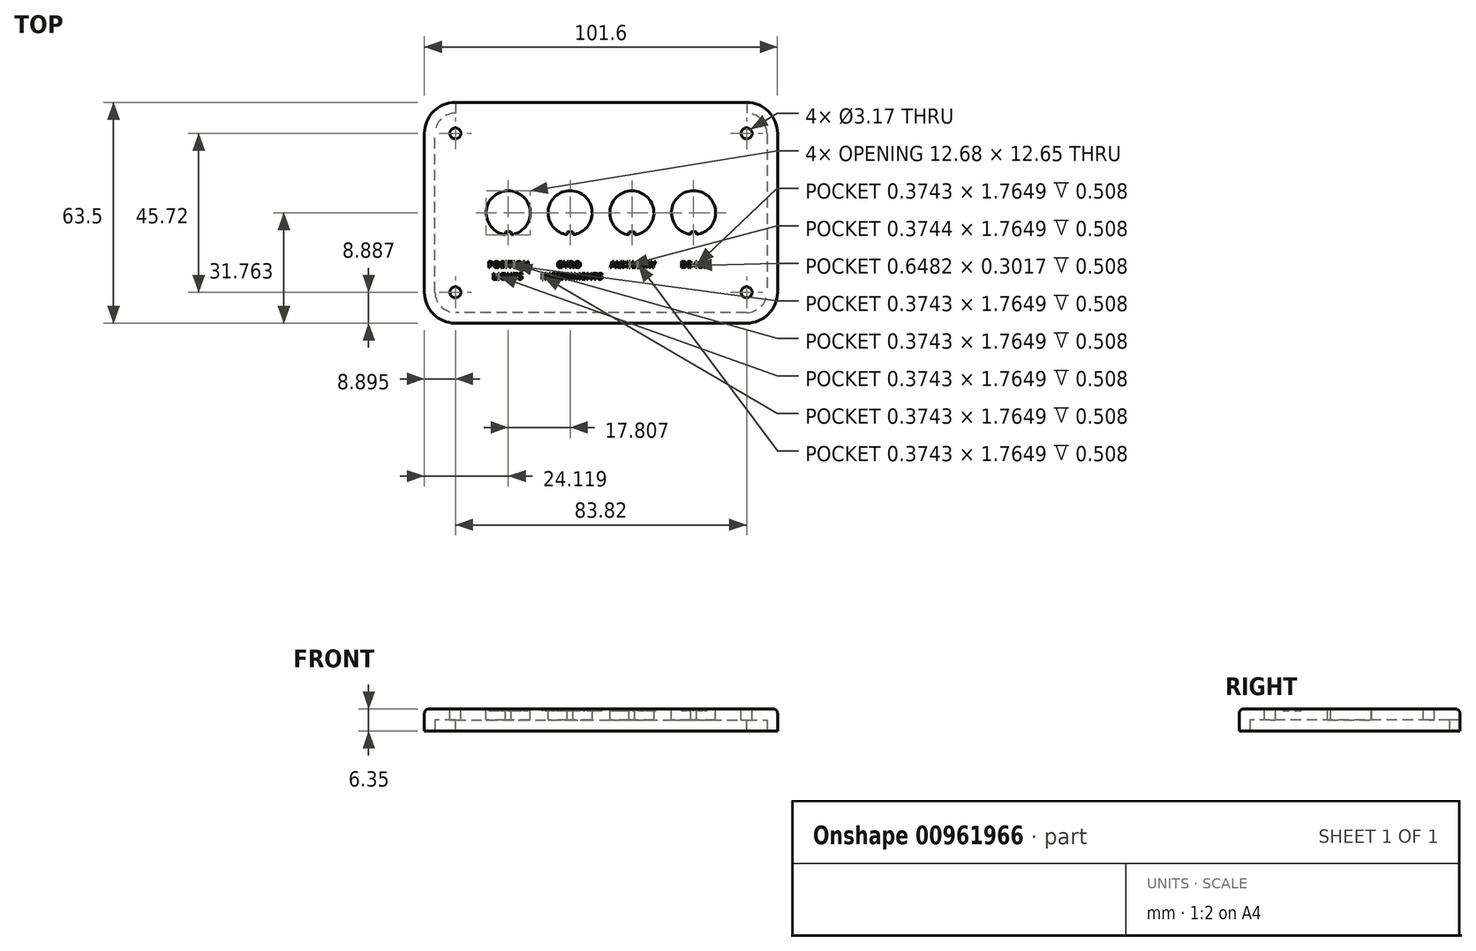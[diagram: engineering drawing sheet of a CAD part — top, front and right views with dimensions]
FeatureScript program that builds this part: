
annotation { "Feature Type Name" : "Feature", "Feature Type Description" : "" }
export const myFeature = defineFeature(function(context is Context, id is Id, definition is map)
    precondition{}
    {
        {
            var Q0;
            Q0=qCreatedBy(makeId("Top.planeOp"),FACE);
            var sketch = newSketch(context, id + "F0", { "sketchPlane" : qUnion([Q0])});
            skPoint(sketch, "E0.middle", {"position": v(-0.12, 0.03) * mm});
            skPoint(sketch, "E1.visualSharp", {"position": v(-44.57, 25.43) * mm});
            skArc(sketch, "E1.filletArc", {"start": v(-42.03, 25.43) * mm, "mid": v(-43.82, 24.68) * mm, "end": v(-44.57, 22.89) * mm});
            skPoint(sketch, "E2.visualSharp", {"position": v(44.33, 25.43) * mm});
            skArc(sketch, "E2.filletArc", {"start": v(44.33, 22.89) * mm, "mid": v(43.6, 24.68) * mm, "end": v(41.8, 25.43) * mm});
            skPoint(sketch, "E3.visualSharp", {"position": v(44.33, -25.37) * mm});
            skArc(sketch, "E3.filletArc", {"start": v(41.8, -25.37) * mm, "mid": v(43.6, -24.63) * mm, "end": v(44.33, -22.83) * mm});
            skPoint(sketch, "E4.visualSharp", {"position": v(-44.57, -25.37) * mm});
            skArc(sketch, "E4.filletArc", {"start": v(-44.57, -22.83) * mm, "mid": v(-43.82, -24.63) * mm, "end": v(-42.03, -25.37) * mm});
            skCircle(sketch, "E5", {"center": v(-42.03, 22.89) * mm, "radius": 1.59 * mm});
            skCircle(sketch, "E6", {"center": v(-42.03, -22.83) * mm, "radius": 1.59 * mm});
            skCircle(sketch, "E7", {"center": v(41.8, -22.83) * mm, "radius": 1.59 * mm});
            skCircle(sketch, "E8", {"center": v(41.8, 22.89) * mm, "radius": 1.59 * mm});
            skArc(sketch, "E9.0", {"start": v(-47.74, -22.83) * mm, "mid": v(-46.07, -26.87) * mm, "end": v(-42.03, -28.55) * mm});
            skLineSegment(sketch, "E9.1", {"start": v(-42.03, -28.55) * mm, "end": v(41.8, -28.55) * mm});
            skLineSegment(sketch, "E9.2", {"start": v(-47.74, -22.83) * mm, "end": v(-47.74, 22.89) * mm});
            skArc(sketch, "E9.3", {"start": v(41.8, -28.55) * mm, "mid": v(45.84, -26.87) * mm, "end": v(47.5, -22.83) * mm});
            skArc(sketch, "E9.4", {"start": v(-42.03, 28.6) * mm, "mid": v(-46.07, 26.93) * mm, "end": v(-47.74, 22.89) * mm});
            skLineSegment(sketch, "E9.5", {"start": v(-42.03, 28.6) * mm, "end": v(41.8, 28.6) * mm});
            skArc(sketch, "E9.6", {"start": v(47.5, 22.89) * mm, "mid": v(45.84, 26.93) * mm, "end": v(41.8, 28.6) * mm});
            skLineSegment(sketch, "E9.7", {"start": v(47.5, -22.83) * mm, "end": v(47.5, 22.89) * mm});
            skArc(sketch, "E10.0", {"start": v(-50.92, -22.83) * mm, "mid": v(-48.31, -29.12) * mm, "end": v(-42.03, -31.72) * mm});
            skLineSegment(sketch, "E10.1", {"start": v(-42.03, -31.72) * mm, "end": v(41.8, -31.72) * mm});
            skLineSegment(sketch, "E10.2", {"start": v(-50.92, -22.83) * mm, "end": v(-50.92, 22.89) * mm});
            skArc(sketch, "E10.3", {"start": v(41.8, -31.72) * mm, "mid": v(48.08, -29.12) * mm, "end": v(50.68, -22.83) * mm});
            skArc(sketch, "E10.4", {"start": v(-42.03, 31.78) * mm, "mid": v(-48.31, 29.17) * mm, "end": v(-50.92, 22.89) * mm});
            skLineSegment(sketch, "E10.5", {"start": v(-42.03, 31.78) * mm, "end": v(41.8, 31.78) * mm});
            skArc(sketch, "E10.6", {"start": v(50.68, 22.89) * mm, "mid": v(48.08, 29.17) * mm, "end": v(41.8, 31.78) * mm});
            skLineSegment(sketch, "E10.7", {"start": v(50.68, -22.83) * mm, "end": v(50.68, 22.89) * mm});
            skPoint(sketch, "E11", {"position": v(-26.79, 0) * mm});
            skPoint(sketch, "E12", {"position": v(-9, 0) * mm});
            skPoint(sketch, "E13", {"position": v(8.77, 0) * mm});
            skPoint(sketch, "E14", {"position": v(26.55, 0) * mm});
            skLineSegment(sketch, "E15.top", {"start": v(27.33, -5.38) * mm, "end": v(25.74, -5.38) * mm});
            skLineSegment(sketch, "E16", {"start": v(25.74, -6.25) * mm, "end": v(25.74, -5.38) * mm});
            skLineSegment(sketch, "E17", {"start": v(27.33, -6.25) * mm, "end": v(27.33, -5.38) * mm});
            skArc(sketch, "E18", {"start": v(27.33, -6.25) * mm, "mid": v(26.54, 6.4) * mm, "end": v(25.74, -6.25) * mm});
            skLineSegment(sketch, "E19.top", {"start": v(9.58, -5.43) * mm, "end": v(7.99, -5.43) * mm});
            skLineSegment(sketch, "E20", {"start": v(7.99, -6.3) * mm, "end": v(7.99, -5.43) * mm});
            skLineSegment(sketch, "E21", {"start": v(9.58, -6.3) * mm, "end": v(9.58, -5.43) * mm});
            skArc(sketch, "E22", {"start": v(9.58, -6.3) * mm, "mid": v(8.78, 6.35) * mm, "end": v(7.99, -6.3) * mm});
            skLineSegment(sketch, "E23.top", {"start": v(-8.2, -5.4) * mm, "end": v(-9.79, -5.4) * mm});
            skLineSegment(sketch, "E24", {"start": v(-9.79, -6.26) * mm, "end": v(-9.79, -5.4) * mm});
            skLineSegment(sketch, "E25", {"start": v(-8.2, -6.26) * mm, "end": v(-8.2, -5.4) * mm});
            skArc(sketch, "E26", {"start": v(-8.2, -6.26) * mm, "mid": v(-9, 6.4) * mm, "end": v(-9.79, -6.26) * mm});
            skLineSegment(sketch, "E27.top", {"start": v(-26, -5.42) * mm, "end": v(-27.6, -5.42) * mm});
            skLineSegment(sketch, "E28", {"start": v(-27.6, -6.28) * mm, "end": v(-27.6, -5.42) * mm});
            skLineSegment(sketch, "E29", {"start": v(-26, -6.28) * mm, "end": v(-26, -5.42) * mm});
            skArc(sketch, "E30", {"start": v(-26, -6.28) * mm, "mid": v(-26.8, 6.37) * mm, "end": v(-27.6, -6.28) * mm});
            skText(sketch, "E31", { "text": "POSITION\n  LIGHTS", "fontName": "OpenSans-Bold.ttf"});
            skText(sketch, "E32", { "text": "       GYRO\nINSTRUMENTS", "fontName": "OpenSans-Bold.ttf"});
            skText(sketch, "E33", { "text": "DE-ICE", "fontName": "OpenSans-Bold.ttf"});
            skText(sketch, "E34", { "text": "AUXILIARY", "fontName": "OpenSans-Bold.ttf"});
            skLineSegment(sketch, "E35", {"start": v(-42.03, 31.78) * mm, "end": v(-42.03, 28.6) * mm});
            skLineSegment(sketch, "E36", {"start": v(41.8, 31.78) * mm, "end": v(41.8, 28.6) * mm});
            const initialGuessF0  = {"E31": [-0.03267, -0.01575, 1, 0, 0.00178], "E32": [-0.0173, -0.01575, 1, 0, 0.00178], "E33": [0.02284, -0.01575, 1, 0, 0.00178], "E34": [0.00253, -0.01575, 1, 0, 0.00178]};
            skSetInitialGuess(sketch, initialGuessF0);
            skSolve(sketch);
        }
        {
            var Q0;
            Q0 = qSketchRegion(id + "F0", true);
            var Q1;
            Q1=makeQuery(id+"F0.imprint","IMPRINT",FACE,{"disambiguationData":[TD([[makeQuery(id+"F0.imprint","IMPRINT",EDGE,{"derivedFrom":sQuery(id+"F0.wireOp",EDGE,"E9.0")}),1.0]])]});
            var Q2;
            Q2=makeQuery(id+"F0.imprint","IMPRINT",FACE,{"disambiguationData":[TD([[makeQuery(id+"F0.imprint","IMPRINT",EDGE,{"derivedFrom":sQuery(id+"F0.wireOp",EDGE,"E31.sketch_text.stroke-0")}),1.0]])]});
            var Q3;
            Q3=makeQuery(id+"F0.imprint","IMPRINT",FACE,{"disambiguationData":[TD([[makeQuery(id+"F0.imprint","IMPRINT",EDGE,{"derivedFrom":sQuery(id+"F0.wireOp",EDGE,"E31.sketch_text.stroke-24")}),1.0]])]});
            var Q4;
            Q4=makeQuery(id+"F0.imprint","IMPRINT",FACE,{"disambiguationData":[TD([[makeQuery(id+"F0.imprint","IMPRINT",EDGE,{"derivedFrom":sQuery(id+"F0.wireOp",EDGE,"E31.sketch_text.stroke-82")}),1.0]])]});
            var Q5;
            Q5=makeQuery(id+"F0.imprint","IMPRINT",FACE,{"disambiguationData":[TD([[makeQuery(id+"F0.imprint","IMPRINT",EDGE,{"derivedFrom":sQuery(id+"F0.wireOp",EDGE,"E33.sketch_text.stroke-7")}),1.0]])]});
            var Q6;
            Q6=makeQuery(id+"F0.imprint","IMPRINT",FACE,{"disambiguationData":[TD([[makeQuery(id+"F0.imprint","IMPRINT",EDGE,{"derivedFrom":sQuery(id+"F0.wireOp",EDGE,"E34.sketch_text.stroke-61")}),1.0]])]});
            var Q7;
            Q7=makeQuery(id+"F0.imprint","IMPRINT",FACE,{"disambiguationData":[TD([[makeQuery(id+"F0.imprint","IMPRINT",EDGE,{"derivedFrom":sQuery(id+"F0.wireOp",EDGE,"E34.sketch_text.stroke-65")}),1.0]])]});
            var Q8;
            Q8=makeQuery(id+"F0.imprint","IMPRINT",FACE,{"disambiguationData":[TD([[makeQuery(id+"F0.imprint","IMPRINT",EDGE,{"derivedFrom":sQuery(id+"F0.wireOp",EDGE,"E32.sketch_text.stroke-28")}),1.0]])]});
            var Q9;
            Q9=makeQuery(id+"F0.imprint","IMPRINT",FACE,{"disambiguationData":[TD([[makeQuery(id+"F0.imprint","IMPRINT",EDGE,{"derivedFrom":sQuery(id+"F0.wireOp",EDGE,"E32.sketch_text.stroke-115")}),1.0]])]});
            var Q10;
            Q10=makeQuery(id+"F0.imprint","IMPRINT",FACE,{"disambiguationData":[TD([[makeQuery(id+"F0.imprint","IMPRINT",EDGE,{"derivedFrom":sQuery(id+"F0.wireOp",EDGE,"E32.sketch_text.stroke-55")}),1.0]])]});
            var Q11;
            Q11=makeQuery(id+"F0.imprint","IMPRINT",FACE,{"disambiguationData":[TD([[makeQuery(id+"F0.imprint","IMPRINT",EDGE,{"derivedFrom":sQuery(id+"F0.wireOp",EDGE,"E34.sketch_text.stroke-8")}),1.0]])]});
            var Q12;
            Q12=makeQuery(id+"F0.imprint","IMPRINT",FACE,{"disambiguationData":[TD([[makeQuery(id+"F0.imprint","IMPRINT",EDGE,{"derivedFrom":sQuery(id+"F0.wireOp",EDGE,"E31.sketch_text.stroke-74")}),-1.0]])]});
            var Q13;
            Q13=makeQuery(id+"F0.imprint","IMPRINT",FACE,{"disambiguationData":[TD([[makeQuery(id+"F0.imprint","IMPRINT",EDGE,{"derivedFrom":sQuery(id+"F0.wireOp",EDGE,"E31.sketch_text.stroke-88")}),-1.0]])]});
            var Q14;
            Q14=makeQuery(id+"F0.imprint","IMPRINT",FACE,{"disambiguationData":[TD([[makeQuery(id+"F0.imprint","IMPRINT",EDGE,{"derivedFrom":sQuery(id+"F0.wireOp",EDGE,"E32.sketch_text.stroke-47")}),-1.0]])]});
            var Q15;
            Q15=makeQuery(id+"F0.imprint","IMPRINT",FACE,{"disambiguationData":[TD([[makeQuery(id+"F0.imprint","IMPRINT",EDGE,{"derivedFrom":sQuery(id+"F0.wireOp",EDGE,"E32.sketch_text.stroke-28")}),-1.0]])]});
            var Q16;
            Q16=makeQuery(id+"F0.imprint","IMPRINT",FACE,{"disambiguationData":[TD([[makeQuery(id+"F0.imprint","IMPRINT",EDGE,{"derivedFrom":sQuery(id+"F0.wireOp",EDGE,"E32.sketch_text.stroke-19")}),-1.0]])]});
            var Q17;
            Q17=makeQuery(id+"F0.imprint","IMPRINT",FACE,{"disambiguationData":[TD([[makeQuery(id+"F0.imprint","IMPRINT",EDGE,{"derivedFrom":sQuery(id+"F0.wireOp",EDGE,"E32.sketch_text.stroke-0")}),-1.0]])]});
            var Q18;
            Q18=makeQuery(id+"F0.imprint","IMPRINT",FACE,{"disambiguationData":[TD([[makeQuery(id+"F0.imprint","IMPRINT",EDGE,{"derivedFrom":sQuery(id+"F0.wireOp",EDGE,"E32.sketch_text.stroke-168")}),-1.0]])]});
            var Q19;
            Q19=makeQuery(id+"F0.imprint","IMPRINT",FACE,{"disambiguationData":[TD([[makeQuery(id+"F0.imprint","IMPRINT",EDGE,{"derivedFrom":sQuery(id+"F0.wireOp",EDGE,"E32.sketch_text.stroke-180")}),-1.0]])]});
            var Q20;
            Q20=makeQuery(id+"F0.imprint","IMPRINT",FACE,{"disambiguationData":[TD([[makeQuery(id+"F0.imprint","IMPRINT",EDGE,{"derivedFrom":sQuery(id+"F0.wireOp",EDGE,"E32.sketch_text.stroke-194")}),-1.0]])]});
            var Q21;
            Q21=makeQuery(id+"F0.imprint","IMPRINT",FACE,{"disambiguationData":[TD([[makeQuery(id+"F0.imprint","IMPRINT",EDGE,{"derivedFrom":sQuery(id+"F0.wireOp",EDGE,"E32.sketch_text.stroke-202")}),-1.0]])]});
            var Q22;
            Q22=makeQuery(id+"F0.imprint","IMPRINT",FACE,{"disambiguationData":[TD([[makeQuery(id+"F0.imprint","IMPRINT",EDGE,{"derivedFrom":sQuery(id+"F0.wireOp",EDGE,"E31.sketch_text.stroke-102")}),-1.0]])]});
            var Q23;
            Q23=makeQuery(id+"F0.imprint","IMPRINT",FACE,{"disambiguationData":[TD([[makeQuery(id+"F0.imprint","IMPRINT",EDGE,{"derivedFrom":sQuery(id+"F0.wireOp",EDGE,"E31.sketch_text.stroke-108")}),-1.0]])]});
            var Q24;
            Q24=makeQuery(id+"F0.imprint","IMPRINT",FACE,{"disambiguationData":[TD([[makeQuery(id+"F0.imprint","IMPRINT",EDGE,{"derivedFrom":sQuery(id+"F0.wireOp",EDGE,"E31.sketch_text.stroke-112")}),-1.0]])]});
            var Q25;
            Q25=makeQuery(id+"F0.imprint","IMPRINT",FACE,{"disambiguationData":[TD([[makeQuery(id+"F0.imprint","IMPRINT",EDGE,{"derivedFrom":sQuery(id+"F0.wireOp",EDGE,"E31.sketch_text.stroke-131")}),-1.0]])]});
            var Q26;
            Q26=makeQuery(id+"F0.imprint","IMPRINT",FACE,{"disambiguationData":[TD([[makeQuery(id+"F0.imprint","IMPRINT",EDGE,{"derivedFrom":sQuery(id+"F0.wireOp",EDGE,"E31.sketch_text.stroke-143")}),-1.0]])]});
            var Q27;
            Q27=makeQuery(id+"F0.imprint","IMPRINT",FACE,{"disambiguationData":[TD([[makeQuery(id+"F0.imprint","IMPRINT",EDGE,{"derivedFrom":sQuery(id+"F0.wireOp",EDGE,"E31.sketch_text.stroke-151")}),-1.0]])]});
            var Q28;
            Q28=makeQuery(id+"F0.imprint","IMPRINT",FACE,{"disambiguationData":[TD([[makeQuery(id+"F0.imprint","IMPRINT",EDGE,{"derivedFrom":sQuery(id+"F0.wireOp",EDGE,"E31.sketch_text.stroke-70")}),-1.0]])]});
            var Q29;
            Q29=makeQuery(id+"F0.imprint","IMPRINT",FACE,{"disambiguationData":[TD([[makeQuery(id+"F0.imprint","IMPRINT",EDGE,{"derivedFrom":sQuery(id+"F0.wireOp",EDGE,"E31.sketch_text.stroke-62")}),-1.0]])]});
            var Q30;
            Q30=makeQuery(id+"F0.imprint","IMPRINT",FACE,{"disambiguationData":[TD([[makeQuery(id+"F0.imprint","IMPRINT",EDGE,{"derivedFrom":sQuery(id+"F0.wireOp",EDGE,"E31.sketch_text.stroke-58")}),-1.0]])]});
            var Q31;
            Q31=makeQuery(id+"F0.imprint","IMPRINT",FACE,{"disambiguationData":[TD([[makeQuery(id+"F0.imprint","IMPRINT",EDGE,{"derivedFrom":sQuery(id+"F0.wireOp",EDGE,"E31.sketch_text.stroke-30")}),-1.0]])]});
            var Q32;
            Q32=makeQuery(id+"F0.imprint","IMPRINT",FACE,{"disambiguationData":[TD([[makeQuery(id+"F0.imprint","IMPRINT",EDGE,{"derivedFrom":sQuery(id+"F0.wireOp",EDGE,"E31.sketch_text.stroke-16")}),-1.0]])]});
            var Q33;
            Q33=makeQuery(id+"F0.imprint","IMPRINT",FACE,{"disambiguationData":[TD([[makeQuery(id+"F0.imprint","IMPRINT",EDGE,{"derivedFrom":sQuery(id+"F0.wireOp",EDGE,"E31.sketch_text.stroke-0")}),-1.0]])]});
            var Q34;
            Q34=makeQuery(id+"F0.imprint","IMPRINT",FACE,{"disambiguationData":[TD([[makeQuery(id+"F0.imprint","IMPRINT",EDGE,{"derivedFrom":sQuery(id+"F0.wireOp",EDGE,"E32.sketch_text.stroke-61")}),-1.0]])]});
            var Q35;
            Q35=makeQuery(id+"F0.imprint","IMPRINT",FACE,{"disambiguationData":[TD([[makeQuery(id+"F0.imprint","IMPRINT",EDGE,{"derivedFrom":sQuery(id+"F0.wireOp",EDGE,"E32.sketch_text.stroke-65")}),-1.0]])]});
            var Q36;
            Q36=makeQuery(id+"F0.imprint","IMPRINT",FACE,{"disambiguationData":[TD([[makeQuery(id+"F0.imprint","IMPRINT",EDGE,{"derivedFrom":sQuery(id+"F0.wireOp",EDGE,"E32.sketch_text.stroke-79")}),-1.0]])]});
            var Q37;
            Q37=makeQuery(id+"F0.imprint","IMPRINT",FACE,{"disambiguationData":[TD([[makeQuery(id+"F0.imprint","IMPRINT",EDGE,{"derivedFrom":sQuery(id+"F0.wireOp",EDGE,"E32.sketch_text.stroke-107")}),-1.0]])]});
            var Q38;
            Q38=makeQuery(id+"F0.imprint","IMPRINT",FACE,{"disambiguationData":[TD([[makeQuery(id+"F0.imprint","IMPRINT",EDGE,{"derivedFrom":sQuery(id+"F0.wireOp",EDGE,"E32.sketch_text.stroke-115")}),-1.0]])]});
            var Q39;
            Q39=makeQuery(id+"F0.imprint","IMPRINT",FACE,{"disambiguationData":[TD([[makeQuery(id+"F0.imprint","IMPRINT",EDGE,{"derivedFrom":sQuery(id+"F0.wireOp",EDGE,"E32.sketch_text.stroke-134")}),-1.0]])]});
            var Q40;
            Q40=makeQuery(id+"F0.imprint","IMPRINT",FACE,{"disambiguationData":[TD([[makeQuery(id+"F0.imprint","IMPRINT",EDGE,{"derivedFrom":sQuery(id+"F0.wireOp",EDGE,"E32.sketch_text.stroke-149")}),-1.0]])]});
            var Q41;
            Q41=makeQuery(id+"F0.imprint","IMPRINT",FACE,{"disambiguationData":[TD([[makeQuery(id+"F0.imprint","IMPRINT",EDGE,{"derivedFrom":sQuery(id+"F0.wireOp",EDGE,"E34.sketch_text.stroke-84")}),-1.0]])]});
            var Q42;
            Q42=makeQuery(id+"F0.imprint","IMPRINT",FACE,{"disambiguationData":[TD([[makeQuery(id+"F0.imprint","IMPRINT",EDGE,{"derivedFrom":sQuery(id+"F0.wireOp",EDGE,"E34.sketch_text.stroke-65")}),-1.0]])]});
            var Q43;
            Q43=makeQuery(id+"F0.imprint","IMPRINT",FACE,{"disambiguationData":[TD([[makeQuery(id+"F0.imprint","IMPRINT",EDGE,{"derivedFrom":sQuery(id+"F0.wireOp",EDGE,"E34.sketch_text.stroke-53")}),-1.0]])]});
            var Q44;
            Q44=makeQuery(id+"F0.imprint","IMPRINT",FACE,{"disambiguationData":[TD([[makeQuery(id+"F0.imprint","IMPRINT",EDGE,{"derivedFrom":sQuery(id+"F0.wireOp",EDGE,"E34.sketch_text.stroke-49")}),-1.0]])]});
            var Q45;
            Q45=makeQuery(id+"F0.imprint","IMPRINT",FACE,{"disambiguationData":[TD([[makeQuery(id+"F0.imprint","IMPRINT",EDGE,{"derivedFrom":sQuery(id+"F0.wireOp",EDGE,"E34.sketch_text.stroke-43")}),-1.0]])]});
            var Q46;
            Q46=makeQuery(id+"F0.imprint","IMPRINT",FACE,{"disambiguationData":[TD([[makeQuery(id+"F0.imprint","IMPRINT",EDGE,{"derivedFrom":sQuery(id+"F0.wireOp",EDGE,"E34.sketch_text.stroke-39")}),-1.0]])]});
            var Q47;
            Q47=makeQuery(id+"F0.imprint","IMPRINT",FACE,{"disambiguationData":[TD([[makeQuery(id+"F0.imprint","IMPRINT",EDGE,{"derivedFrom":sQuery(id+"F0.wireOp",EDGE,"E34.sketch_text.stroke-27")}),-1.0]])]});
            var Q48;
            Q48=makeQuery(id+"F0.imprint","IMPRINT",FACE,{"disambiguationData":[TD([[makeQuery(id+"F0.imprint","IMPRINT",EDGE,{"derivedFrom":sQuery(id+"F0.wireOp",EDGE,"E34.sketch_text.stroke-12")}),-1.0]])]});
            var Q49;
            Q49=makeQuery(id+"F0.imprint","IMPRINT",FACE,{"disambiguationData":[TD([[makeQuery(id+"F0.imprint","IMPRINT",EDGE,{"derivedFrom":sQuery(id+"F0.wireOp",EDGE,"E34.sketch_text.stroke-0")}),-1.0]])]});
            var Q50;
            Q50=makeQuery(id+"F0.imprint","IMPRINT",FACE,{"disambiguationData":[TD([[makeQuery(id+"F0.imprint","IMPRINT",EDGE,{"derivedFrom":sQuery(id+"F0.wireOp",EDGE,"E33.sketch_text.stroke-0")}),-1.0]])]});
            var Q51;
            Q51=makeQuery(id+"F0.imprint","IMPRINT",FACE,{"disambiguationData":[TD([[makeQuery(id+"F0.imprint","IMPRINT",EDGE,{"derivedFrom":sQuery(id+"F0.wireOp",EDGE,"E33.sketch_text.stroke-12")}),-1.0]])]});
            var Q52;
            Q52=makeQuery(id+"F0.imprint","IMPRINT",FACE,{"disambiguationData":[TD([[makeQuery(id+"F0.imprint","IMPRINT",EDGE,{"derivedFrom":sQuery(id+"F0.wireOp",EDGE,"E33.sketch_text.stroke-24")}),-1.0]])]});
            var Q53;
            Q53=makeQuery(id+"F0.imprint","IMPRINT",FACE,{"disambiguationData":[TD([[makeQuery(id+"F0.imprint","IMPRINT",EDGE,{"derivedFrom":sQuery(id+"F0.wireOp",EDGE,"E33.sketch_text.stroke-28")}),-1.0]])]});
            var Q54;
            Q54=makeQuery(id+"F0.imprint","IMPRINT",FACE,{"disambiguationData":[TD([[makeQuery(id+"F0.imprint","IMPRINT",EDGE,{"derivedFrom":sQuery(id+"F0.wireOp",EDGE,"E33.sketch_text.stroke-32")}),-1.0]])]});
            var Q55;
            Q55=makeQuery(id+"F0.imprint","IMPRINT",FACE,{"disambiguationData":[TD([[makeQuery(id+"F0.imprint","IMPRINT",EDGE,{"derivedFrom":sQuery(id+"F0.wireOp",EDGE,"E33.sketch_text.stroke-47")}),-1.0]])]});
            extrude(context, id + "F1", {"entities" : qUnion([Q0, Q1, Q2, Q3, Q4, Q5, Q6, Q7, Q8, Q9, Q10, Q11, Q12, Q13, Q14, Q15, Q16, Q17, Q18, Q19, Q20, Q21, Q22, Q23, Q24, Q25, Q26, Q27, Q28, Q29, Q30, Q31, Q32, Q33, Q34, Q35, Q36, Q37, Q38, Q39, Q40, Q41, Q42, Q43, Q44, Q45, Q46, Q47, Q48, Q49, Q50, Q51, Q52, Q53, Q54, Q55]), "oppositeDirection" : true, "depth" : 6.35 * mm, "offsetDistance" : 25.4 * mm});
        }
        {
            var Q0;
            Q0=makeQuery(id+"F1.opExtrude","CAP_EDGE",EDGE,{"disambiguationData":[OSD([sQuery(id+"F0.wireOp",EDGE,"E10.7")])],"isStart":true});
            fillet(context, id + "F2", {"entities" : qUnion([Q0]), "radius" : 1.27 * mm, "tangentPropagation" : true, "allowEdgeOverflow" : false});
        }
        {
            var Q0;
            Q0=makeQuery(id+"F0.imprint","IMPRINT",FACE,{"disambiguationData":[TD([[makeQuery(id+"F0.imprint","IMPRINT",EDGE,{"derivedFrom":sQuery(id+"F0.wireOp",EDGE,"E31.sketch_text.stroke-16")}),-1.0]])]});
            var Q1;
            Q1=makeQuery(id+"F0.imprint","IMPRINT",FACE,{"disambiguationData":[TD([[makeQuery(id+"F0.imprint","IMPRINT",EDGE,{"derivedFrom":sQuery(id+"F0.wireOp",EDGE,"E31.sketch_text.stroke-0")}),-1.0]])]});
            var Q2;
            Q2=makeQuery(id+"F0.imprint","IMPRINT",FACE,{"disambiguationData":[TD([[makeQuery(id+"F0.imprint","IMPRINT",EDGE,{"derivedFrom":sQuery(id+"F0.wireOp",EDGE,"E31.sketch_text.stroke-30")}),-1.0]])]});
            var Q3;
            Q3=makeQuery(id+"F0.imprint","IMPRINT",FACE,{"disambiguationData":[TD([[makeQuery(id+"F0.imprint","IMPRINT",EDGE,{"derivedFrom":sQuery(id+"F0.wireOp",EDGE,"E31.sketch_text.stroke-58")}),-1.0]])]});
            var Q4;
            Q4=makeQuery(id+"F0.imprint","IMPRINT",FACE,{"disambiguationData":[TD([[makeQuery(id+"F0.imprint","IMPRINT",EDGE,{"derivedFrom":sQuery(id+"F0.wireOp",EDGE,"E31.sketch_text.stroke-62")}),-1.0]])]});
            var Q5;
            Q5=makeQuery(id+"F0.imprint","IMPRINT",FACE,{"disambiguationData":[TD([[makeQuery(id+"F0.imprint","IMPRINT",EDGE,{"derivedFrom":sQuery(id+"F0.wireOp",EDGE,"E31.sketch_text.stroke-70")}),-1.0]])]});
            var Q6;
            Q6=makeQuery(id+"F0.imprint","IMPRINT",FACE,{"disambiguationData":[TD([[makeQuery(id+"F0.imprint","IMPRINT",EDGE,{"derivedFrom":sQuery(id+"F0.wireOp",EDGE,"E31.sketch_text.stroke-131")}),-1.0]])]});
            var Q7;
            Q7=makeQuery(id+"F0.imprint","IMPRINT",FACE,{"disambiguationData":[TD([[makeQuery(id+"F0.imprint","IMPRINT",EDGE,{"derivedFrom":sQuery(id+"F0.wireOp",EDGE,"E31.sketch_text.stroke-112")}),-1.0]])]});
            var Q8;
            Q8=makeQuery(id+"F0.imprint","IMPRINT",FACE,{"disambiguationData":[TD([[makeQuery(id+"F0.imprint","IMPRINT",EDGE,{"derivedFrom":sQuery(id+"F0.wireOp",EDGE,"E31.sketch_text.stroke-108")}),-1.0]])]});
            var Q9;
            Q9=makeQuery(id+"F0.imprint","IMPRINT",FACE,{"disambiguationData":[TD([[makeQuery(id+"F0.imprint","IMPRINT",EDGE,{"derivedFrom":sQuery(id+"F0.wireOp",EDGE,"E31.sketch_text.stroke-102")}),-1.0]])]});
            var Q10;
            Q10=makeQuery(id+"F0.imprint","IMPRINT",FACE,{"disambiguationData":[TD([[makeQuery(id+"F0.imprint","IMPRINT",EDGE,{"derivedFrom":sQuery(id+"F0.wireOp",EDGE,"E31.sketch_text.stroke-74")}),-1.0]])]});
            var Q11;
            Q11=makeQuery(id+"F0.imprint","IMPRINT",FACE,{"disambiguationData":[TD([[makeQuery(id+"F0.imprint","IMPRINT",EDGE,{"derivedFrom":sQuery(id+"F0.wireOp",EDGE,"E31.sketch_text.stroke-88")}),-1.0]])]});
            var Q12;
            Q12=makeQuery(id+"F0.imprint","IMPRINT",FACE,{"disambiguationData":[TD([[makeQuery(id+"F0.imprint","IMPRINT",EDGE,{"derivedFrom":sQuery(id+"F0.wireOp",EDGE,"E31.sketch_text.stroke-143")}),-1.0]])]});
            var Q13;
            Q13=makeQuery(id+"F0.imprint","IMPRINT",FACE,{"disambiguationData":[TD([[makeQuery(id+"F0.imprint","IMPRINT",EDGE,{"derivedFrom":sQuery(id+"F0.wireOp",EDGE,"E31.sketch_text.stroke-151")}),-1.0]])]});
            var Q14;
            Q14=makeQuery(id+"F0.imprint","IMPRINT",FACE,{"disambiguationData":[TD([[makeQuery(id+"F0.imprint","IMPRINT",EDGE,{"derivedFrom":sQuery(id+"F0.wireOp",EDGE,"E32.sketch_text.stroke-28")}),-1.0]])]});
            var Q15;
            Q15=makeQuery(id+"F0.imprint","IMPRINT",FACE,{"disambiguationData":[TD([[makeQuery(id+"F0.imprint","IMPRINT",EDGE,{"derivedFrom":sQuery(id+"F0.wireOp",EDGE,"E32.sketch_text.stroke-19")}),-1.0]])]});
            var Q16;
            Q16=makeQuery(id+"F0.imprint","IMPRINT",FACE,{"disambiguationData":[TD([[makeQuery(id+"F0.imprint","IMPRINT",EDGE,{"derivedFrom":sQuery(id+"F0.wireOp",EDGE,"E32.sketch_text.stroke-0")}),-1.0]])]});
            var Q17;
            Q17=makeQuery(id+"F0.imprint","IMPRINT",FACE,{"disambiguationData":[TD([[makeQuery(id+"F0.imprint","IMPRINT",EDGE,{"derivedFrom":sQuery(id+"F0.wireOp",EDGE,"E32.sketch_text.stroke-134")}),-1.0]])]});
            var Q18;
            Q18=makeQuery(id+"F0.imprint","IMPRINT",FACE,{"disambiguationData":[TD([[makeQuery(id+"F0.imprint","IMPRINT",EDGE,{"derivedFrom":sQuery(id+"F0.wireOp",EDGE,"E32.sketch_text.stroke-115")}),-1.0]])]});
            var Q19;
            Q19=makeQuery(id+"F0.imprint","IMPRINT",FACE,{"disambiguationData":[TD([[makeQuery(id+"F0.imprint","IMPRINT",EDGE,{"derivedFrom":sQuery(id+"F0.wireOp",EDGE,"E32.sketch_text.stroke-79")}),-1.0]])]});
            var Q20;
            Q20=makeQuery(id+"F0.imprint","IMPRINT",FACE,{"disambiguationData":[TD([[makeQuery(id+"F0.imprint","IMPRINT",EDGE,{"derivedFrom":sQuery(id+"F0.wireOp",EDGE,"E32.sketch_text.stroke-65")}),-1.0]])]});
            var Q21;
            Q21=makeQuery(id+"F0.imprint","IMPRINT",FACE,{"disambiguationData":[TD([[makeQuery(id+"F0.imprint","IMPRINT",EDGE,{"derivedFrom":sQuery(id+"F0.wireOp",EDGE,"E32.sketch_text.stroke-61")}),-1.0]])]});
            var Q22;
            Q22=makeQuery(id+"F0.imprint","IMPRINT",FACE,{"disambiguationData":[TD([[makeQuery(id+"F0.imprint","IMPRINT",EDGE,{"derivedFrom":sQuery(id+"F0.wireOp",EDGE,"E32.sketch_text.stroke-107")}),-1.0]])]});
            var Q23;
            Q23=makeQuery(id+"F0.imprint","IMPRINT",FACE,{"disambiguationData":[TD([[makeQuery(id+"F0.imprint","IMPRINT",EDGE,{"derivedFrom":sQuery(id+"F0.wireOp",EDGE,"E32.sketch_text.stroke-47")}),-1.0]])]});
            var Q24;
            Q24=makeQuery(id+"F0.imprint","IMPRINT",FACE,{"disambiguationData":[TD([[makeQuery(id+"F0.imprint","IMPRINT",EDGE,{"derivedFrom":sQuery(id+"F0.wireOp",EDGE,"E32.sketch_text.stroke-149")}),-1.0]])]});
            var Q25;
            Q25=makeQuery(id+"F0.imprint","IMPRINT",FACE,{"disambiguationData":[TD([[makeQuery(id+"F0.imprint","IMPRINT",EDGE,{"derivedFrom":sQuery(id+"F0.wireOp",EDGE,"E32.sketch_text.stroke-168")}),-1.0]])]});
            var Q26;
            Q26=makeQuery(id+"F0.imprint","IMPRINT",FACE,{"disambiguationData":[TD([[makeQuery(id+"F0.imprint","IMPRINT",EDGE,{"derivedFrom":sQuery(id+"F0.wireOp",EDGE,"E32.sketch_text.stroke-180")}),-1.0]])]});
            var Q27;
            Q27=makeQuery(id+"F0.imprint","IMPRINT",FACE,{"disambiguationData":[TD([[makeQuery(id+"F0.imprint","IMPRINT",EDGE,{"derivedFrom":sQuery(id+"F0.wireOp",EDGE,"E32.sketch_text.stroke-194")}),-1.0]])]});
            var Q28;
            Q28=makeQuery(id+"F0.imprint","IMPRINT",FACE,{"disambiguationData":[TD([[makeQuery(id+"F0.imprint","IMPRINT",EDGE,{"derivedFrom":sQuery(id+"F0.wireOp",EDGE,"E32.sketch_text.stroke-202")}),-1.0]])]});
            var Q29;
            Q29=makeQuery(id+"F0.imprint","IMPRINT",FACE,{"disambiguationData":[TD([[makeQuery(id+"F0.imprint","IMPRINT",EDGE,{"derivedFrom":sQuery(id+"F0.wireOp",EDGE,"E34.sketch_text.stroke-84")}),-1.0]])]});
            var Q30;
            Q30=makeQuery(id+"F0.imprint","IMPRINT",FACE,{"disambiguationData":[TD([[makeQuery(id+"F0.imprint","IMPRINT",EDGE,{"derivedFrom":sQuery(id+"F0.wireOp",EDGE,"E34.sketch_text.stroke-65")}),-1.0]])]});
            var Q31;
            Q31=makeQuery(id+"F0.imprint","IMPRINT",FACE,{"disambiguationData":[TD([[makeQuery(id+"F0.imprint","IMPRINT",EDGE,{"derivedFrom":sQuery(id+"F0.wireOp",EDGE,"E34.sketch_text.stroke-53")}),-1.0]])]});
            var Q32;
            Q32=makeQuery(id+"F0.imprint","IMPRINT",FACE,{"disambiguationData":[TD([[makeQuery(id+"F0.imprint","IMPRINT",EDGE,{"derivedFrom":sQuery(id+"F0.wireOp",EDGE,"E34.sketch_text.stroke-49")}),-1.0]])]});
            var Q33;
            Q33=makeQuery(id+"F0.imprint","IMPRINT",FACE,{"disambiguationData":[TD([[makeQuery(id+"F0.imprint","IMPRINT",EDGE,{"derivedFrom":sQuery(id+"F0.wireOp",EDGE,"E34.sketch_text.stroke-43")}),-1.0]])]});
            var Q34;
            Q34=makeQuery(id+"F0.imprint","IMPRINT",FACE,{"disambiguationData":[TD([[makeQuery(id+"F0.imprint","IMPRINT",EDGE,{"derivedFrom":sQuery(id+"F0.wireOp",EDGE,"E34.sketch_text.stroke-39")}),-1.0]])]});
            var Q35;
            Q35=makeQuery(id+"F0.imprint","IMPRINT",FACE,{"disambiguationData":[TD([[makeQuery(id+"F0.imprint","IMPRINT",EDGE,{"derivedFrom":sQuery(id+"F0.wireOp",EDGE,"E34.sketch_text.stroke-27")}),-1.0]])]});
            var Q36;
            Q36=makeQuery(id+"F0.imprint","IMPRINT",FACE,{"disambiguationData":[TD([[makeQuery(id+"F0.imprint","IMPRINT",EDGE,{"derivedFrom":sQuery(id+"F0.wireOp",EDGE,"E34.sketch_text.stroke-12")}),-1.0]])]});
            var Q37;
            Q37=makeQuery(id+"F0.imprint","IMPRINT",FACE,{"disambiguationData":[TD([[makeQuery(id+"F0.imprint","IMPRINT",EDGE,{"derivedFrom":sQuery(id+"F0.wireOp",EDGE,"E34.sketch_text.stroke-0")}),-1.0]])]});
            var Q38;
            Q38=makeQuery(id+"F0.imprint","IMPRINT",FACE,{"disambiguationData":[TD([[makeQuery(id+"F0.imprint","IMPRINT",EDGE,{"derivedFrom":sQuery(id+"F0.wireOp",EDGE,"E33.sketch_text.stroke-0")}),-1.0]])]});
            var Q39;
            Q39=makeQuery(id+"F0.imprint","IMPRINT",FACE,{"disambiguationData":[TD([[makeQuery(id+"F0.imprint","IMPRINT",EDGE,{"derivedFrom":sQuery(id+"F0.wireOp",EDGE,"E33.sketch_text.stroke-12")}),-1.0]])]});
            var Q40;
            Q40=makeQuery(id+"F0.imprint","IMPRINT",FACE,{"disambiguationData":[TD([[makeQuery(id+"F0.imprint","IMPRINT",EDGE,{"derivedFrom":sQuery(id+"F0.wireOp",EDGE,"E33.sketch_text.stroke-24")}),-1.0]])]});
            var Q41;
            Q41=makeQuery(id+"F0.imprint","IMPRINT",FACE,{"disambiguationData":[TD([[makeQuery(id+"F0.imprint","IMPRINT",EDGE,{"derivedFrom":sQuery(id+"F0.wireOp",EDGE,"E33.sketch_text.stroke-28")}),-1.0]])]});
            var Q42;
            Q42=makeQuery(id+"F0.imprint","IMPRINT",FACE,{"disambiguationData":[TD([[makeQuery(id+"F0.imprint","IMPRINT",EDGE,{"derivedFrom":sQuery(id+"F0.wireOp",EDGE,"E33.sketch_text.stroke-32")}),-1.0]])]});
            var Q43;
            Q43=makeQuery(id+"F0.imprint","IMPRINT",FACE,{"disambiguationData":[TD([[makeQuery(id+"F0.imprint","IMPRINT",EDGE,{"derivedFrom":sQuery(id+"F0.wireOp",EDGE,"E33.sketch_text.stroke-47")}),-1.0]])]});
            extrude(context, id + "F3", {"entities" : qUnion([Q0, Q1, Q2, Q3, Q4, Q5, Q6, Q7, Q8, Q9, Q10, Q11, Q12, Q13, Q14, Q15, Q16, Q17, Q18, Q19, Q20, Q21, Q22, Q23, Q24, Q25, Q26, Q27, Q28, Q29, Q30, Q31, Q32, Q33, Q34, Q35, Q36, Q37, Q38, Q39, Q40, Q41, Q42, Q43]), "operationType" : NewBodyOperationType.REMOVE, "oppositeDirection" : true, "depth" : 0.5 * mm, "offsetDistance" : 25.4 * mm});
        }
        {
            var Q0;
            Q0=makeQuery(id+"F1.opExtrude","CAP_FACE",FACE,{"disambiguationData":[OSD([sQuery(id+"F0.wireOp",EDGE,"E5"),sQuery(id+"F0.wireOp",EDGE,"E6"),sQuery(id+"F0.wireOp",EDGE,"E7"),sQuery(id+"F0.wireOp",EDGE,"E8"),sQuery(id+"F0.wireOp",EDGE,"E10.0"),sQuery(id+"F0.wireOp",EDGE,"E10.1"),sQuery(id+"F0.wireOp",EDGE,"E10.2"),sQuery(id+"F0.wireOp",EDGE,"E10.3"),sQuery(id+"F0.wireOp",EDGE,"E10.4"),sQuery(id+"F0.wireOp",EDGE,"E10.5"),sQuery(id+"F0.wireOp",EDGE,"E10.6"),sQuery(id+"F0.wireOp",EDGE,"E10.7"),sQuery(id+"F0.wireOp",EDGE,"E15.top"),sQuery(id+"F0.wireOp",EDGE,"E16"),sQuery(id+"F0.wireOp",EDGE,"E17"),sQuery(id+"F0.wireOp",EDGE,"E18"),sQuery(id+"F0.wireOp",EDGE,"E19.top"),sQuery(id+"F0.wireOp",EDGE,"E20"),sQuery(id+"F0.wireOp",EDGE,"E21"),sQuery(id+"F0.wireOp",EDGE,"E22"),sQuery(id+"F0.wireOp",EDGE,"E23.top"),sQuery(id+"F0.wireOp",EDGE,"E24"),sQuery(id+"F0.wireOp",EDGE,"E25"),sQuery(id+"F0.wireOp",EDGE,"E26"),sQuery(id+"F0.wireOp",EDGE,"E27.top"),sQuery(id+"F0.wireOp",EDGE,"E28"),sQuery(id+"F0.wireOp",EDGE,"E29"),sQuery(id+"F0.wireOp",EDGE,"E30")])],"isStart":false});
            var sketch = newSketch(context, id + "F4", { "sketchPlane" : qUnion([Q0])});
            skLineSegment(sketch, "E37.0", {"start": v(47.64, -22.89) * mm, "end": v(47.64, 22.83) * mm});
            skArc(sketch, "E37.1", {"start": v(41.8, -28.73) * mm, "mid": v(45.93, -27.02) * mm, "end": v(47.64, -22.89) * mm});
            skArc(sketch, "E37.2", {"start": v(47.64, 22.83) * mm, "mid": v(45.93, 26.96) * mm, "end": v(41.8, 28.67) * mm});
            skLineSegment(sketch, "E37.3", {"start": v(-42.03, -28.73) * mm, "end": v(41.8, -28.73) * mm});
            skLineSegment(sketch, "E37.4", {"start": v(41.8, 28.67) * mm, "end": v(-42.03, 28.67) * mm});
            skArc(sketch, "E37.5", {"start": v(-42.03, 28.67) * mm, "mid": v(-46.16, 26.96) * mm, "end": v(-47.87, 22.83) * mm});
            skLineSegment(sketch, "E37.6", {"start": v(-47.87, 22.83) * mm, "end": v(-47.87, -22.89) * mm});
            skArc(sketch, "E37.7", {"start": v(-47.87, -22.89) * mm, "mid": v(-46.16, -27.02) * mm, "end": v(-42.03, -28.73) * mm});
            skSolve(sketch);
        }
        {
            var Q0;
            Q0 = qSketchRegion(id + "F4", true);
            extrude(context, id + "F5", {"entities" : qUnion([Q0]), "operationType" : NewBodyOperationType.REMOVE, "oppositeDirection" : true, "depth" : 3.17 * mm, "offsetDistance" : 25.4 * mm});
        }
        {
            var Q0;
            Q0=makeQuery(id+"F1.opExtrude","CAP_FACE",FACE,{"disambiguationData":[OSD([sQuery(id+"F0.wireOp",EDGE,"E5"),sQuery(id+"F0.wireOp",EDGE,"E6"),sQuery(id+"F0.wireOp",EDGE,"E7"),sQuery(id+"F0.wireOp",EDGE,"E8"),sQuery(id+"F0.wireOp",EDGE,"E10.0"),sQuery(id+"F0.wireOp",EDGE,"E10.1"),sQuery(id+"F0.wireOp",EDGE,"E10.2"),sQuery(id+"F0.wireOp",EDGE,"E10.3"),sQuery(id+"F0.wireOp",EDGE,"E10.4"),sQuery(id+"F0.wireOp",EDGE,"E10.5"),sQuery(id+"F0.wireOp",EDGE,"E10.6"),sQuery(id+"F0.wireOp",EDGE,"E10.7"),sQuery(id+"F0.wireOp",EDGE,"E15.top"),sQuery(id+"F0.wireOp",EDGE,"E16"),sQuery(id+"F0.wireOp",EDGE,"E17"),sQuery(id+"F0.wireOp",EDGE,"E18"),sQuery(id+"F0.wireOp",EDGE,"E19.top"),sQuery(id+"F0.wireOp",EDGE,"E20"),sQuery(id+"F0.wireOp",EDGE,"E21"),sQuery(id+"F0.wireOp",EDGE,"E22"),sQuery(id+"F0.wireOp",EDGE,"E23.top"),sQuery(id+"F0.wireOp",EDGE,"E24"),sQuery(id+"F0.wireOp",EDGE,"E25"),sQuery(id+"F0.wireOp",EDGE,"E26"),sQuery(id+"F0.wireOp",EDGE,"E27.top"),sQuery(id+"F0.wireOp",EDGE,"E28"),sQuery(id+"F0.wireOp",EDGE,"E29"),sQuery(id+"F0.wireOp",EDGE,"E30")])],"isStart":false});
            var sketch = newSketch(context, id + "F6", { "sketchPlane" : qUnion([Q0])});
            skLineSegment(sketch, "E38", {"start": v(-42.03, -31.78) * mm, "end": v(-42.03, -28.73) * mm});
            skLineSegment(sketch, "E39", {"start": v(41.8, -31.78) * mm, "end": v(41.8, -28.73) * mm});
            skSolve(sketch);
        }
        {
            var Q0;
            Q0 = qSketchRegion(id + "F6", true);
            var Q1;
            Q1=makeQuery(id+"F6.imprint","IMPRINT",FACE,{"disambiguationData":[TD([[makeQuery(id+"F6.imprint","IMPRINT",EDGE,{"derivedFrom":sQuery(id+"F6.wireOp",EDGE,"E38")}),-1.0]])]});
            extrude(context, id + "F7", {"entities" : qUnion([Q0, Q1]), "operationType" : NewBodyOperationType.REMOVE, "oppositeDirection" : true, "depth" : 3.17 * mm, "offsetDistance" : 25.4 * mm});
        }
    });
